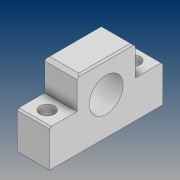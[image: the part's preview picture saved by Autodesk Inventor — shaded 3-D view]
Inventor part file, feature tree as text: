
AUTODESK INVENTOR PART (.ipt)
format: ipt  version: 2021 (Build 250183000, 183)  size: 132,608 bytes
history: native  units: mm
features: chamfer x3, sketch x2, projected_geometry x2, extrude x1, hole x1
ambient origin geometry x8: Origin, YZ Plane, XZ Plane, XY Plane, X Axis, Y Axis, Z Axis, Center Point
bodies: Solid1 (feature_tree)
feature tree (9):
  extrude  "Extrusion1"  Depth=70.0mm
  hole  "Hole1"  [1 undecoded]
  chamfer  "Chamfer1"  Distance=21.0mm
  chamfer  "Chamfer2"  Distance=20.0mm
  chamfer  "Chamfer3"  Distance=1.0mm Angle=45.0deg
  sketch  "Sketch1"  dims[d0=36.0mm d1=70.0mm]
  sketch  "Sketch2"  dims[d2=19.0mm d3=24.0mm d4=21.0mm d5=20.0mm d6=0.0mm d7=9.0mm d8=6.0mm d9=4.0mm d10=2.0mm d11=90.0deg d12=8.0mm d13=20.594885mm d14=1.0mm d15=2.0mm d16=45.0deg d17=1.0mm d18=2.0mm d19=45.0deg d20=2.0mm d21=2.0mm d22=45.0deg]
  projected_geometry  "Projected Loop1"
  projected_geometry  "Projected Loop2"
note: 1 required parameter value undecoded (feature->parameter linkage not recoverable at this tier; creation-order binding heuristic only, values carry confidence <= 0.55)
